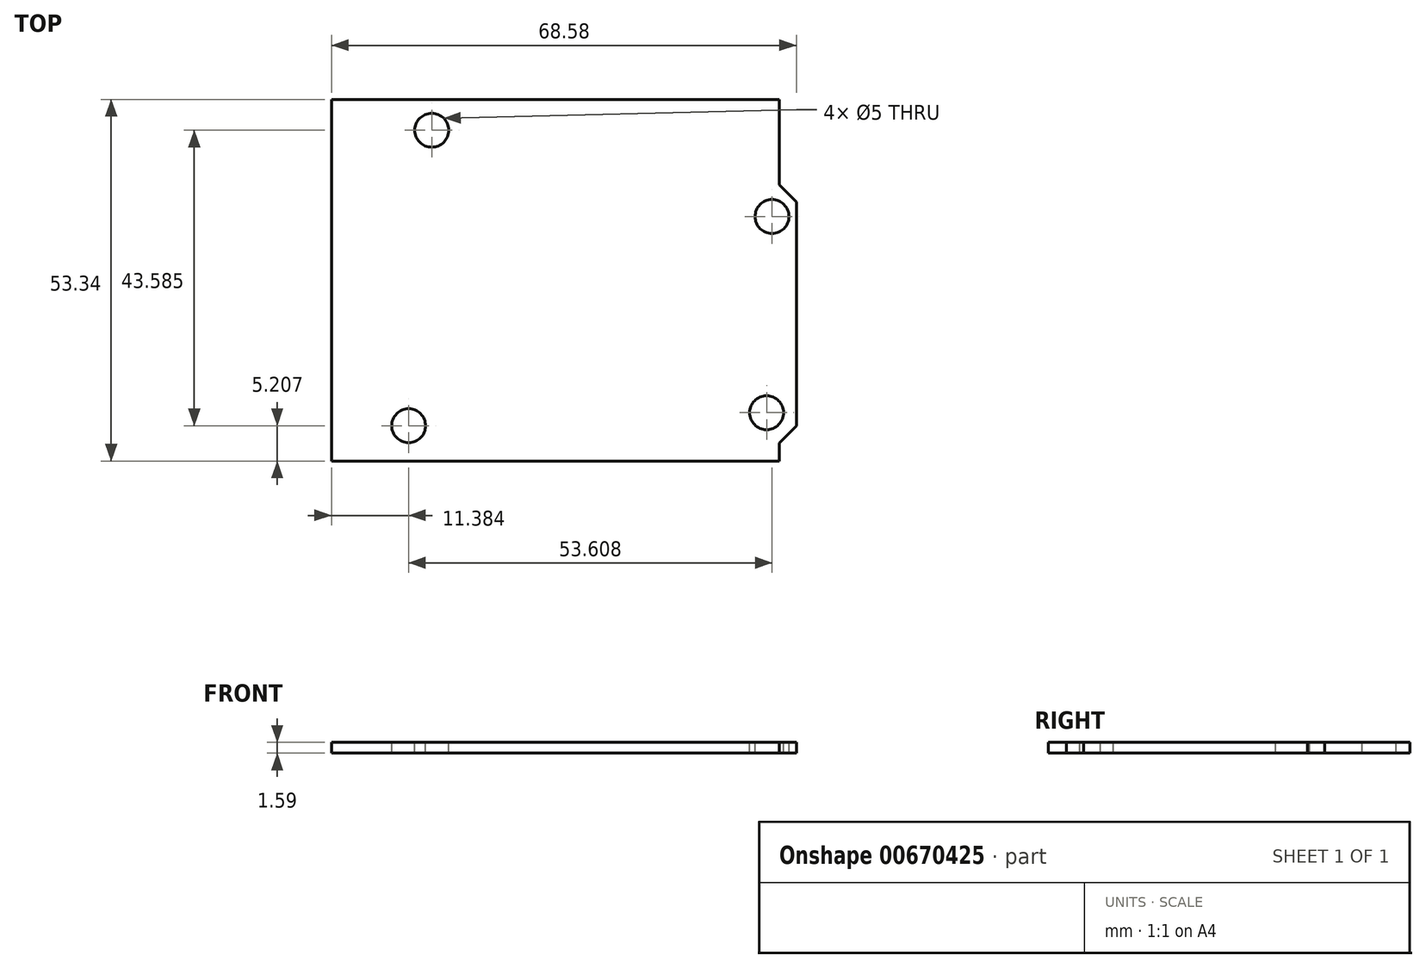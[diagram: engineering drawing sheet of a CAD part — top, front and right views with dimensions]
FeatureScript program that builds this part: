
annotation { "Feature Type Name" : "Feature", "Feature Type Description" : "" }
export const myFeature = defineFeature(function(context is Context, id is Id, definition is map)
    precondition{}
    {
        {
            var Q0;
            Q0=qCreatedBy(makeId("Top.planeOp"),FACE);
            var sketch = newSketch(context, id + "F0", { "sketchPlane" : qUnion([Q0])});
            skLineSegment(sketch, "E0", {"start": v(-33.02, 26.67) * mm, "end": v(33.02, 26.67) * mm});
            skLineSegment(sketch, "E1", {"start": v(33.02, 26.67) * mm, "end": v(33.02, 14.1) * mm});
            skLineSegment(sketch, "E2", {"start": v(33.02, -26.67) * mm, "end": v(-33.02, -26.67) * mm});
            skLineSegment(sketch, "E3", {"start": v(-33.02, -26.67) * mm, "end": v(-33.02, 26.67) * mm});
            skLineSegment(sketch, "E4", {"start": v(33.02, -24) * mm, "end": v(35.56, -21.46) * mm});
            skLineSegment(sketch, "E5", {"start": v(35.56, -21.46) * mm, "end": v(35.56, 11.56) * mm});
            skLineSegment(sketch, "E6", {"start": v(35.56, 11.56) * mm, "end": v(33.02, 14.1) * mm});
            skLineSegment(sketch, "E7", {"start": v(0, 0) * mm, "end": v(0, 26.67) * mm, "construction": true});
            skLineSegment(sketch, "E8", {"start": v(0, 0) * mm, "end": v(-33.02, 0) * mm, "construction": true});
            skLineSegment(sketch, "E9.trimOffspring", {"start": v(33.02, -24) * mm, "end": v(33.02, -26.67) * mm});
            skLineSegment(sketch, "E10", {"start": v(33.02, 14.1) * mm, "end": v(33.02, -24) * mm});
            skSolve(sketch);
        }
        {
            var Q0;
            Q0 = qSketchRegion(id + "F0", true);
            extrude(context, id + "F1", {"entities" : qUnion([Q0]), "depth" : 1.59 * mm, "offsetDistance" : 25 * mm});
        }
        {
            var Q0;
            Q0=makeQuery(id+"F1.opExtrude","CAP_FACE",FACE,{"disambiguationData":[OSD([sQuery(id+"F0.wireOp",EDGE,"E0"),sQuery(id+"F0.wireOp",EDGE,"E1"),sQuery(id+"F0.wireOp",EDGE,"E2"),sQuery(id+"F0.wireOp",EDGE,"E3"),sQuery(id+"F0.wireOp",EDGE,"E4"),sQuery(id+"F0.wireOp",EDGE,"E5"),sQuery(id+"F0.wireOp",EDGE,"E6"),sQuery(id+"F0.wireOp",EDGE,"E9.trimOffspring")])],"isStart":false});
            var sketch = newSketch(context, id + "F2", { "sketchPlane" : qUnion([Q0])});
            skCircle(sketch, "E11", {"center": v(-18.22, 22.12) * mm, "radius": 2.5 * mm});
            skCircle(sketch, "E12", {"center": v(31.97, 9.4) * mm, "radius": 2.5 * mm});
            skCircle(sketch, "E13", {"center": v(31.17, -19.55) * mm, "radius": 2.5 * mm});
            skCircle(sketch, "E14", {"center": v(-21.64, -21.46) * mm, "radius": 2.5 * mm});
            skSolve(sketch);
        }
        {
            var Q0;
            Q0 = qSketchRegion(id + "F2", true);
            extrude(context, id + "F3", {"entities" : qUnion([Q0]), "operationType" : NewBodyOperationType.REMOVE, "endBound" : BoundingType.THROUGH_ALL, "oppositeDirection" : true, "depth" : 25 * mm, "offsetDistance" : 25 * mm});
        }
    });
